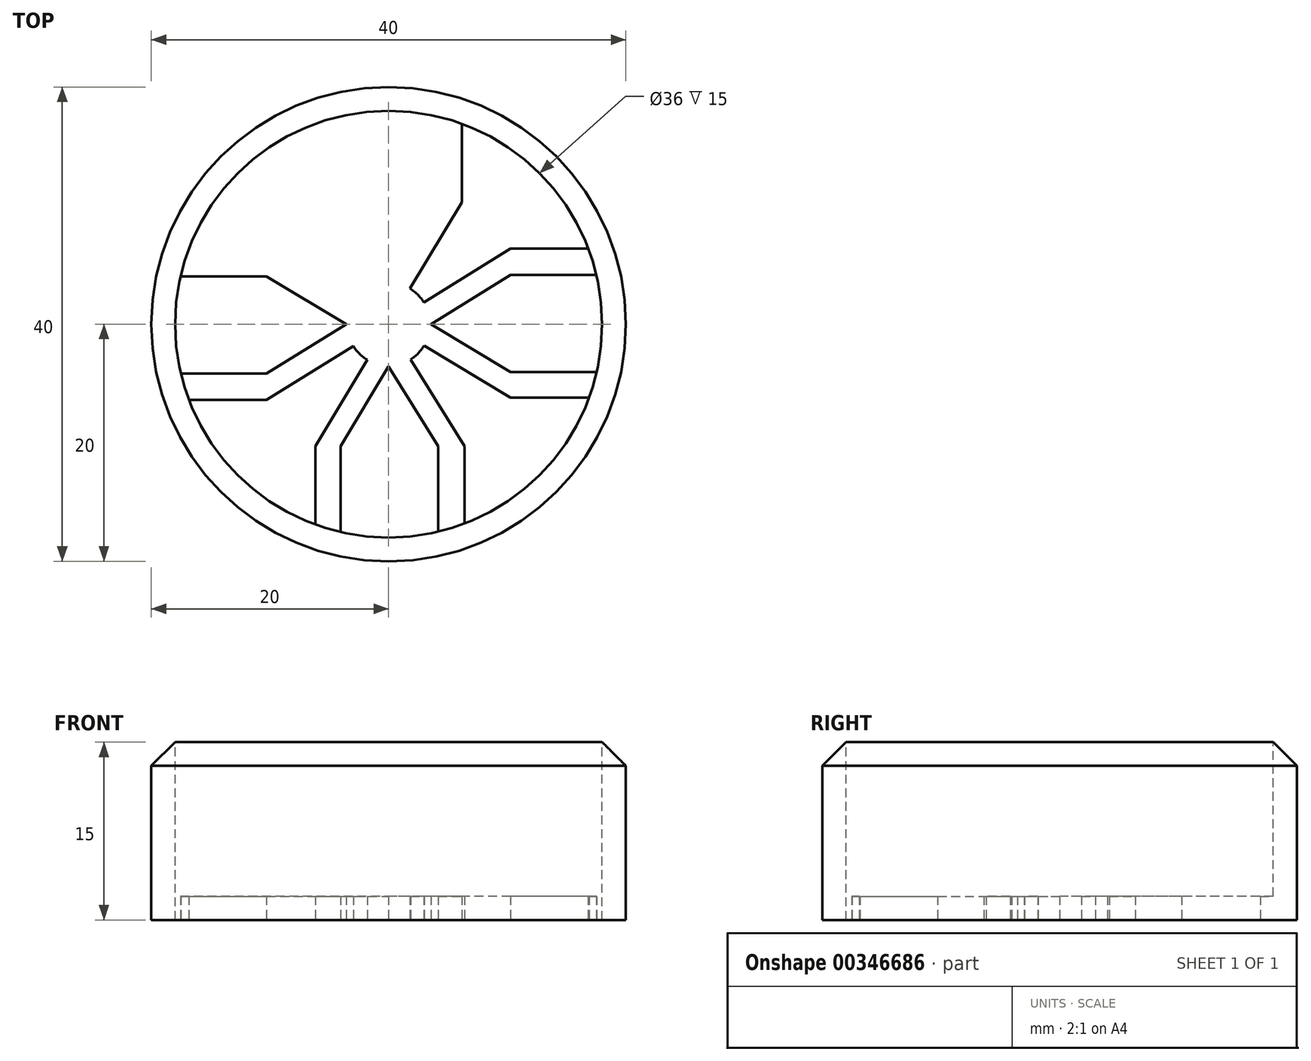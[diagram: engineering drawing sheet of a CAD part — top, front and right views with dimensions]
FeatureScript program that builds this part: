
annotation { "Feature Type Name" : "Feature", "Feature Type Description" : "" }
export const myFeature = defineFeature(function(context is Context, id is Id, definition is map)
    precondition{}
    {
        {
            var Q0;
            Q0=qCreatedBy(makeId("Top.planeOp"),FACE);
            var sketch = newSketch(context, id + "F0", { "sketchPlane" : qUnion([Q0])});
            skCircle(sketch, "E0", {"center": v(0, 0) * mm, "radius": 20 * mm});
            skSolve(sketch);
        }
        {
            var Q0;
            Q0=makeQuery(id+"F0.imprint","IMPRINT",FACE,{"disambiguationData":[TD([[makeQuery(id+"F0.imprint","IMPRINT",EDGE,{"derivedFrom":sQuery(id+"F0.wireOp",EDGE,"E0")}),1.0]])]});
            extrude(context, id + "F1", {"entities" : qUnion([Q0]), "depth" : 15 * mm});
        }
        {
            var Q0;
            Q0=makeQuery(id+"F1.opExtrude","CAP_FACE",FACE,{"disambiguationData":[OSD([sQuery(id+"F0.wireOp",EDGE,"E0")])],"isStart":false});
            var sketch = newSketch(context, id + "F2", { "sketchPlane" : qUnion([Q0])});
            skCircle(sketch, "E1", {"center": v(0, 0) * mm, "radius": 18 * mm});
            skSolve(sketch);
        }
        {
            var Q0;
            Q0=makeQuery(id+"F2.imprint","IMPRINT",FACE,{"disambiguationData":[TD([[makeQuery(id+"F2.imprint","IMPRINT",EDGE,{"derivedFrom":sQuery(id+"F2.wireOp",EDGE,"E1")}),1.0]])]});
            extrude(context, id + "F3", {"entities" : qUnion([Q0]), "operationType" : NewBodyOperationType.REMOVE, "oppositeDirection" : true, "depth" : 13 * mm});
        }
        {
            var Q0;
            Q0=makeQuery(id+"F3.boolean.opBoolean","COPY",FACE,{"derivedFrom":makeQuery(id+"F3.opExtrude","CAP_FACE",FACE,{"disambiguationData":[OSD([sQuery(id+"F2.wireOp",EDGE,"E1")])],"isStart":false})});
            var sketch = newSketch(context, id + "F4", { "sketchPlane" : qUnion([Q0])});
            skCircle(sketch, "E2", {"center": v(0, 0) * mm, "radius": 1.5 * mm});
            skCircle(sketch, "E3", {"center": v(0, 0) * mm, "radius": 3.5 * mm});
            skSolve(sketch);
        }
        {
            var Q0;
            Q0=sQuery(id+"F4.wireOp",EDGE,"E2");
            var Q1;
            Q1=sQuery(id+"F4.wireOp",EDGE,"E3");
            extrude(context, id + "F5", {"bodyType" : ToolBodyType.SURFACE, "surfaceEntities" : qUnion([Q0, Q1]), "depth" : 16 * mm});
        }
        {
            var Q0;
            Q0=makeQuery(id+"F1.opExtrude","CAP_FACE",FACE,{"disambiguationData":[OSD([sQuery(id+"F0.wireOp",EDGE,"E0")])],"isStart":true});
            var sketch = newSketch(context, id + "F6", { "sketchPlane" : qUnion([Q0])});
            skCircle(sketch, "E4", {"center": v(0, 0) * mm, "radius": 18 * mm});
            skCircle(sketch, "E5", {"center": v(0, 0) * mm, "radius": 3.5 * mm});
            skSolve(sketch);
        }
        {
            var Q0;
            Q0=makeQuery(id+"F6.imprint","IMPRINT",FACE,{"disambiguationData":[TD([[makeQuery(id+"F6.imprint","IMPRINT",EDGE,{"derivedFrom":sQuery(id+"F6.wireOp",EDGE,"E4")}),1.0]])]});
            var sketch = newSketch(context, id + "F7", { "sketchPlane" : qUnion([Q0])});
            skLineSegment(sketch, "E6", {"start": v(0, 0) * mm, "end": v(-6.18, 10.29) * mm});
            skLineSegment(sketch, "E7", {"start": v(0, 0) * mm, "end": v(6.39, 10.29) * mm});
            skLineSegment(sketch, "E8", {"start": v(-6.18, 10.29) * mm, "end": v(-6.18, 18.48) * mm});
            skLineSegment(sketch, "E9", {"start": v(6.39, 10.29) * mm, "end": v(6.39, 18.48) * mm});
            skLineSegment(sketch, "E10", {"start": v(0, 3.57) * mm, "end": v(-4.04, 10.29) * mm});
            skLineSegment(sketch, "E11", {"start": v(-4.04, 10.29) * mm, "end": v(-4.04, 18.48) * mm});
            skLineSegment(sketch, "E12", {"start": v(0, 3.57) * mm, "end": v(4.17, 10.29) * mm});
            skLineSegment(sketch, "E13", {"start": v(4.17, 10.29) * mm, "end": v(4.17, 18.48) * mm});
            skLineSegment(sketch, "E14.1.0", {"start": v(10.29, 6.18) * mm, "end": v(18.48, 6.18) * mm});
            skLineSegment(sketch, "E14.1.1", {"start": v(10.29, 4.04) * mm, "end": v(18.48, 4.04) * mm});
            skLineSegment(sketch, "E14.1.2", {"start": v(3.57, 0) * mm, "end": v(10.29, 4.04) * mm});
            skLineSegment(sketch, "E14.1.3", {"start": v(0, 0) * mm, "end": v(10.29, 6.18) * mm});
            skLineSegment(sketch, "E14.1.4", {"start": v(0, 0) * mm, "end": v(10.29, -6.39) * mm});
            skLineSegment(sketch, "E14.1.5", {"start": v(3.57, 0) * mm, "end": v(10.29, -4.17) * mm});
            skLineSegment(sketch, "E14.1.6", {"start": v(10.29, -4.17) * mm, "end": v(18.48, -4.17) * mm});
            skLineSegment(sketch, "E14.1.7", {"start": v(10.29, -6.39) * mm, "end": v(18.48, -6.39) * mm});
            skLineSegment(sketch, "E14.2.0", {"start": v(6.18, -10.29) * mm, "end": v(6.18, -18.48) * mm});
            skLineSegment(sketch, "E14.2.1", {"start": v(4.04, -10.29) * mm, "end": v(4.04, -18.48) * mm});
            skLineSegment(sketch, "E14.2.2", {"start": v(0, -3.57) * mm, "end": v(4.04, -10.29) * mm});
            skLineSegment(sketch, "E14.2.3", {"start": v(0, 0) * mm, "end": v(6.18, -10.29) * mm});
            skLineSegment(sketch, "E14.2.4", {"start": v(0, 0) * mm, "end": v(-6.39, -10.29) * mm});
            skLineSegment(sketch, "E14.2.5", {"start": v(0, -3.57) * mm, "end": v(-4.17, -10.29) * mm});
            skLineSegment(sketch, "E14.2.6", {"start": v(-4.17, -10.29) * mm, "end": v(-4.17, -18.48) * mm});
            skLineSegment(sketch, "E14.2.7", {"start": v(-6.39, -10.29) * mm, "end": v(-6.39, -18.48) * mm});
            skPoint(sketch, "E14.center", {"position": v(0, 0) * mm});
            skLineSegment(sketch, "E14.anchor1", {"start": v(0, 0) * mm, "end": v(-6.18, 10.29) * mm, "construction": true});
            skLineSegment(sketch, "E14.anchor2", {"start": v(0, 0) * mm, "end": v(6.18, -10.29) * mm, "construction": true});
            skLineSegment(sketch, "E15.2.0", {"start": v(0, 0) * mm, "end": v(-10.29, 6.39) * mm});
            skLineSegment(sketch, "E15.2.1", {"start": v(-3.57, 0) * mm, "end": v(-10.29, 4.17) * mm});
            skLineSegment(sketch, "E15.2.2", {"start": v(-3.57, 0) * mm, "end": v(-10.29, -4.04) * mm});
            skLineSegment(sketch, "E15.2.3", {"start": v(0, 0) * mm, "end": v(-10.29, -6.18) * mm});
            skLineSegment(sketch, "E15.2.4", {"start": v(-10.29, -4.04) * mm, "end": v(-18.48, -4.04) * mm});
            skLineSegment(sketch, "E15.2.5", {"start": v(-10.29, -6.18) * mm, "end": v(-18.48, -6.18) * mm});
            skLineSegment(sketch, "E15.2.6", {"start": v(-10.29, 4.17) * mm, "end": v(-18.48, 4.17) * mm});
            skLineSegment(sketch, "E15.2.7", {"start": v(-10.29, 6.39) * mm, "end": v(-18.48, 6.39) * mm});
            skLineSegment(sketch, "E15.anchor1", {"start": v(0, 0) * mm, "end": v(10.29, -6.39) * mm, "construction": true});
            skLineSegment(sketch, "E15.anchor2", {"start": v(0, 0) * mm, "end": v(-10.29, 6.39) * mm, "construction": true});
            skSolve(sketch);
        }
        {
            var Q0;
            {var subQ5=sQuery(id+"F7.wireOp",EDGE,"E14.2.5");Q0=makeQuery(id+"F7.imprint","IMPRINT",FACE,{"disambiguationData":[TD([[makeQuery(id+"F7.imprint","IMPRINT",EDGE,{"derivedFrom":subQ5}),1.0]])]});}
            var Q1;
            {var subQ7=sQuery(id+"F7.wireOp",EDGE,"E14.2.7");var subQ8=sQuery(id+"F7.wireOp",EDGE,"E14.2.4");var subQ9=makeQuery(id+"F7.imprint","INTERSECT",VERTEX,{"derivedFrom":[subQ8,subQ7]});Q1=makeQuery(id+"F7.imprint","IMPRINT",FACE,{"disambiguationData":[TD([[makeQuery(id+"F7.imprint","IMPRINT",EDGE,{"disambiguationData":[TD([[subQ9,1.0]])],"derivedFrom":subQ8}),-1.0]])]});}
            var Q2;
            {var subQ5=sQuery(id+"F7.wireOp",EDGE,"E15.2.1");Q2=makeQuery(id+"F7.imprint","IMPRINT",FACE,{"disambiguationData":[TD([[makeQuery(id+"F7.imprint","IMPRINT",EDGE,{"derivedFrom":subQ5}),1.0]])]});}
            var Q3;
            {var subQ5=sQuery(id+"F7.wireOp",EDGE,"E8");var subQ6=sQuery(id+"F7.wireOp",EDGE,"E6");var subQ7=makeQuery(id+"F7.imprint","INTERSECT",VERTEX,{"derivedFrom":[subQ6,subQ5]});Q3=makeQuery(id+"F7.imprint","IMPRINT",FACE,{"disambiguationData":[TD([[makeQuery(id+"F7.imprint","IMPRINT",EDGE,{"disambiguationData":[TD([[subQ7,1.0]])],"derivedFrom":subQ6}),1.0]])]});}
            var Q4;
            {var subQ5=sQuery(id+"F7.wireOp",EDGE,"E10");Q4=makeQuery(id+"F7.imprint","IMPRINT",FACE,{"disambiguationData":[TD([[makeQuery(id+"F7.imprint","IMPRINT",EDGE,{"derivedFrom":subQ5}),-1.0]])]});}
            var Q5;
            {var subQ5=sQuery(id+"F7.wireOp",EDGE,"E9");var subQ6=sQuery(id+"F7.wireOp",EDGE,"E7");var subQ7=makeQuery(id+"F7.imprint","INTERSECT",VERTEX,{"derivedFrom":[subQ6,subQ5]});Q5=makeQuery(id+"F7.imprint","IMPRINT",FACE,{"disambiguationData":[TD([[makeQuery(id+"F7.imprint","IMPRINT",EDGE,{"disambiguationData":[TD([[subQ7,1.0]])],"derivedFrom":subQ6}),-1.0]])]});}
            var Q6;
            {var subQ4=sQuery(id+"F7.wireOp",EDGE,"E14.1.2");Q6=makeQuery(id+"F7.imprint","IMPRINT",FACE,{"disambiguationData":[TD([[makeQuery(id+"F7.imprint","IMPRINT",EDGE,{"derivedFrom":subQ4}),-1.0]])]});}
            var Q7;
            {var subQ5=sQuery(id+"F7.wireOp",EDGE,"E14.1.7");var subQ6=sQuery(id+"F7.wireOp",EDGE,"E14.1.4");var subQ7=makeQuery(id+"F7.imprint","INTERSECT",VERTEX,{"derivedFrom":[subQ6,subQ5]});Q7=makeQuery(id+"F7.imprint","IMPRINT",FACE,{"disambiguationData":[TD([[makeQuery(id+"F7.imprint","IMPRINT",EDGE,{"disambiguationData":[TD([[subQ7,1.0]])],"derivedFrom":subQ6}),-1.0]])]});}
            extrude(context, id + "F8", {"entities" : qUnion([Q0, Q1, Q2, Q3, Q4, Q5, Q6, Q7]), "operationType" : NewBodyOperationType.REMOVE, "oppositeDirection" : true, "depth" : 25 * mm});
        }
        {
            var Q0;
            Q0=makeQuery(id+"F1.opExtrude","CAP_EDGE",EDGE,{"disambiguationData":[OSD([sQuery(id+"F0.wireOp",EDGE,"E0")])],"isStart":false});
            chamfer(context, id + "F9", {"entities" : qUnion([Q0]), "chamferType" : ChamferType.TWO_OFFSETS, "width1" : 2 * mm, "oppositeDirection" : false, "width2" : 2 * mm, "tangentPropagation" : true});
        }
    });
